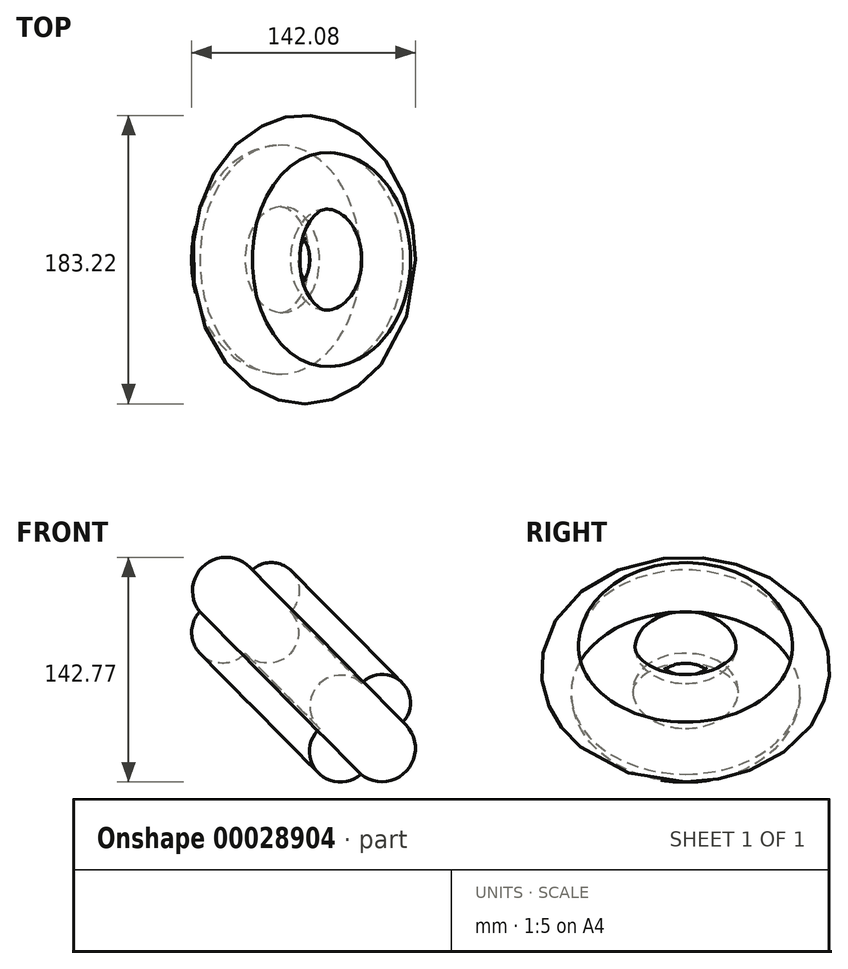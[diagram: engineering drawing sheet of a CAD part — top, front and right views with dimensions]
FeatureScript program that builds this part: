
annotation { "Feature Type Name" : "Feature", "Feature Type Description" : "" }
export const myFeature = defineFeature(function(context is Context, id is Id, definition is map)
    precondition{}
    {
        {
            var Q0;
            Q0=qCreatedBy(makeId("Front.planeOp"),FACE);
            var sketch = newSketch(context, id + "F0", { "sketchPlane" : qUnion([Q0])});
            skLineSegment(sketch, "E0", {"start": v(76.54, 0) * mm, "end": v(0, -75.82) * mm});
            skPoint(sketch, "E1.orphan", {"position": v(0, 52.91) * mm});
            skPoint(sketch, "E2.orphan", {"position": v(57.62, 52.91) * mm});
            skPoint(sketch, "E3.orphan", {"position": v(57.62, 0) * mm});
            skPoint(sketch, "E4.left.start.orphan", {"position": v(0, 0) * mm});
            skArc(sketch, "E5", {"start": v(33.32, 52.91) * mm, "mid": v(3.43, 56.35) * mm, "end": v(0, 26.46) * mm});
            skArc(sketch, "E6", {"start": v(57.62, 26.46) * mm, "mid": v(58.7, 51.83) * mm, "end": v(33.32, 52.91) * mm});
            skArc(sketch, "E7", {"start": v(28.8, 0) * mm, "mid": v(56.44, -1.18) * mm, "end": v(57.62, 26.46) * mm});
            skArc(sketch, "E8", {"start": v(0, 26.46) * mm, "mid": v(1.18, -1.18) * mm, "end": v(28.8, 0) * mm});
            skSolve(sketch);
        }
        {
            var Q0;
            Q0 = qSketchRegion(id + "F0", true);
            var Q1;
            Q1=sQuery(id+"F0.wireOp",EDGE,"E0");
            revolve(context, id + "F1", {"entities" : qUnion([Q0]), "axis" : qUnion([Q1]), "revolveType" : RevolveType.FULL});
        }
    });
